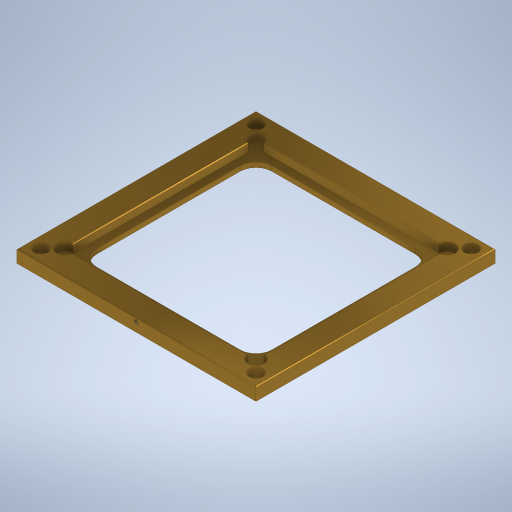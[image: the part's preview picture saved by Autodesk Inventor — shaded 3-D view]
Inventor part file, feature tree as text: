
AUTODESK INVENTOR PART (.ipt)
format: ipt  version: 2023 (Build 270158000, 158)  size: 374,272 bytes
history: native  units: mm
features: sketch x6, extrude x4, hole x2, other x1, chamfer x1
ambient origin geometry x8: Origin, YZ Plane, XZ Plane, XY Plane, X Axis, Y Axis, Z Axis, Center Point
bodies: Body1 (feature_tree)
feature tree (14):
  other  "Sólido1"
  extrude  "Extrusão1"  Depth=150.0mm
  extrude  "Extrusão2"  Depth=120.0mm
  extrude  "Extrusão3"  TaperAngle=0.0deg  [1 undecoded]
  extrude  "Extrusão4"  Depth=5.0mm TaperAngle=0.0deg
  hole  "Furo1"  [1 undecoded]
  hole  "Furo2"  [1 undecoded]
  chamfer  "Chamfer1"  Distance=10.0mm
  sketch  "Esboço1"  dims[d0=150.0mm d1=150.0mm]
  sketch  "Esboço2"  dims[d2=8.0mm d3=0.0mm d4=120.0mm]
  sketch  "Esboço3"  dims[d5=120.0mm d6=0.0mm]
  sketch  "Esboço4"  dims[d7=0.0mm d8=5.0mm d9=0.0mm]
  sketch  "Esboço5"  dims[d10=110.0mm d11=0.0mm]
  sketch  "Esboço6"  dims[d12=0.0mm d13=3.0mm d14=0.0mm d15=10.0mm d16=0.0mm d17=0.0mm d18=0.0mm d19=0.0mm d20=0.0mm d21=0.0mm d22=0.0mm d23=0.0mm d24=5.0mm d25=0.0mm d26=5.0mm d27=2.5mm d28=0.0mm d29=2.459mm d30=100.0mm d31=4.0mm d32=2.0mm d33=90.0deg d34=8.8mm d35=20.594885mm d36=7.5mm d37=15.0mm d38=7.5mm d39=7.5mm d40=7.5mm d41=7.5mm d42=7.5mm d43=7.5mm d44=7.5mm d45=5.0mm d46=10.0mm d47=8.5mm d48=5.0mm d49=90.0deg d50=8.0mm d51=20.594885mm d52=10.0mm d53=0.5mm d54=2.0mm d55=45.0deg]
note: 3 required parameter values undecoded (feature->parameter linkage not recoverable at this tier; creation-order binding heuristic only, values carry confidence <= 0.55)
